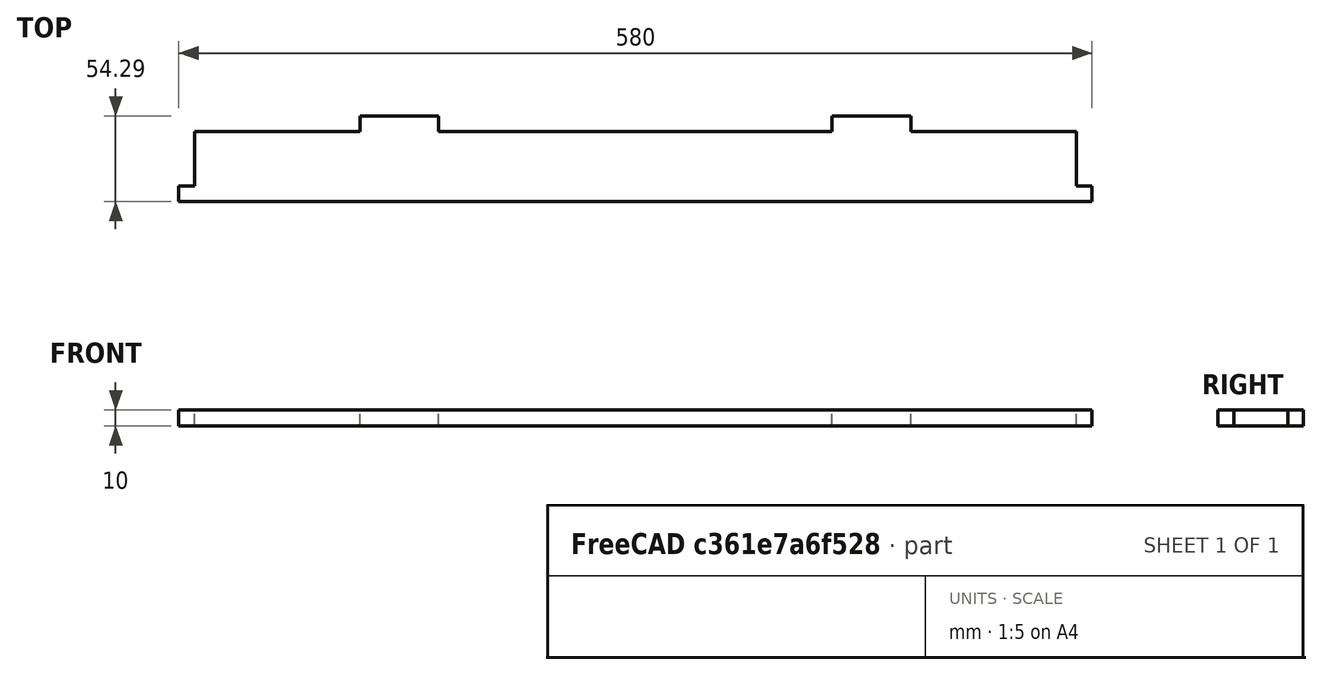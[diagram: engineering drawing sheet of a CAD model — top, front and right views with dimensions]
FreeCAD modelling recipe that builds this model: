
FCSTD DOCUMENT  (FreeCAD 0.16R)
Label: marquee_bottom
License: All rights reserved
LicenseURL: http://fr.wikipedia.org/wiki/<copyright redacted>
objects: Sketcher::SketchObject×1, PartDesign::Pad×1
note: 3 computed .brp shape members not serialized (recipe doc carries the construction recipe); baked Part::Feature solids carry a one-line shape summary decoded from their .brp

FEATURE [Sketcher::SketchObject] Sketch
  sketch-geometry (18):
    g0: LineSegment StartX=0 StartY=0 StartZ=0 EndX=-10 EndY=0 EndZ=0
    g1: LineSegment StartX=-10 StartY=0 StartZ=0 EndX=-10 EndY=10 EndZ=0
    g2: LineSegment StartX=0 StartY=44.2929 StartZ=0 EndX=105 EndY=44.2929 EndZ=0
    g3: LineSegment StartX=105 StartY=44.2929 StartZ=0 EndX=105 EndY=54.2929 EndZ=0
    g4: LineSegment StartX=105 StartY=54.2929 StartZ=0 EndX=155 EndY=54.2929 EndZ=0
    g5: LineSegment StartX=155 StartY=54.2929 StartZ=0 EndX=155 EndY=44.2929 EndZ=0
    g6: LineSegment StartX=405 StartY=44.2929 StartZ=0 EndX=405 EndY=54.2929 EndZ=0
    g7: LineSegment StartX=405 StartY=54.2929 StartZ=0 EndX=455 EndY=54.2929 EndZ=0
    g8: LineSegment StartX=455 StartY=54.2929 StartZ=0 EndX=455 EndY=44.2929 EndZ=0
    g9: LineSegment StartX=455 StartY=44.2929 StartZ=0 EndX=560 EndY=44.2929 EndZ=0
    g10: LineSegment StartX=570 StartY=10 StartZ=0 EndX=570 EndY=0 EndZ=0
    g11: LineSegment StartX=570 StartY=0 StartZ=0 EndX=0 EndY=0 EndZ=0
    g12: LineSegment StartX=-10 StartY=10 StartZ=0 EndX=0 EndY=10 EndZ=0
    g13: LineSegment StartX=0 StartY=10 StartZ=0 EndX=0 EndY=44.2929 EndZ=0
    g14: LineSegment StartX=560 StartY=44.2929 StartZ=0 EndX=560 EndY=10 EndZ=0
    g15: LineSegment StartX=560 StartY=10 StartZ=0 EndX=570 EndY=10 EndZ=0
    g16: LineSegment StartX=155 StartY=44.2929 StartZ=0 EndX=280 EndY=44.2929 EndZ=0
    g17: LineSegment StartX=280 StartY=44.2929 StartZ=0 EndX=405 EndY=44.2929 EndZ=0
  constraints (54):
    c: Coincident(g-1,g0)
    c: Coincident(g0,g1)
    c: Horizontal(g2)
    c: Coincident(g2,g3)
    c: Vertical(g3)
    c: Coincident(g3,g4)
    c: Horizontal(g4)
    c: Coincident(g4,g5)
    c: Vertical(g5)
    c: Vertical(g6)
    c: Coincident(g6,g7)
    c: Horizontal(g7)
    c: Coincident(g7,g8)
    c: Vertical(g8)
    c: Coincident(g8,g9)
    c: Horizontal(g9)
    c: PointOnObject(g10,g-1)
    c: Vertical(g10)
    c: Coincident(g10,g11)
    c: Coincident(g11,g0)
    c: Horizontal(g0)
    c: Vertical(g1)
    c: Equal(g10,g1)
    c: Equal(g4,g7)
    c: Distance(g4) = 50
    c: PointOnObject(g2,g-2)
    c: Coincident(g1,g12)
    c: PointOnObject(g12,g-2)
    c: Coincident(g12,g13)
    c: Coincident(g13,g2)
    c: Coincident(g9,g14)
    c: Vertical(g14)
    c: Coincident(g14,g15)
    c: Coincident(g15,g10)
    c: Horizontal(g15)
    c: Equal(g12,g15)
    c: Horizontal(g12)
    c: Equal(g10,g15)
    c: Equal(g15,g1)
    c: Equal(g2,g9)
    c: DistanceX(g2,g9) = 560
    c: Coincident(g5,g16)
    c: Horizontal(g16)
    c: Coincident(g16,g17)
    c: Coincident(g17,g6)
    c: Horizontal(g17)
    c: Equal(g17,g16)
    c: DistanceX(g5,g6) = 250
    c: Equal(g3,g5)
    c: Equal(g5,g6)
    c: Equal(g6,g8)
    c: DistanceY(g0,g3) = 54.2929
    c: Equal(g8,g10)
    c: Distance(g10) = 10
FEATURE [PartDesign::Pad] Pad
  Length = 10
  Length2 = 100
  Sketch = -> Sketch
  Type = 0
